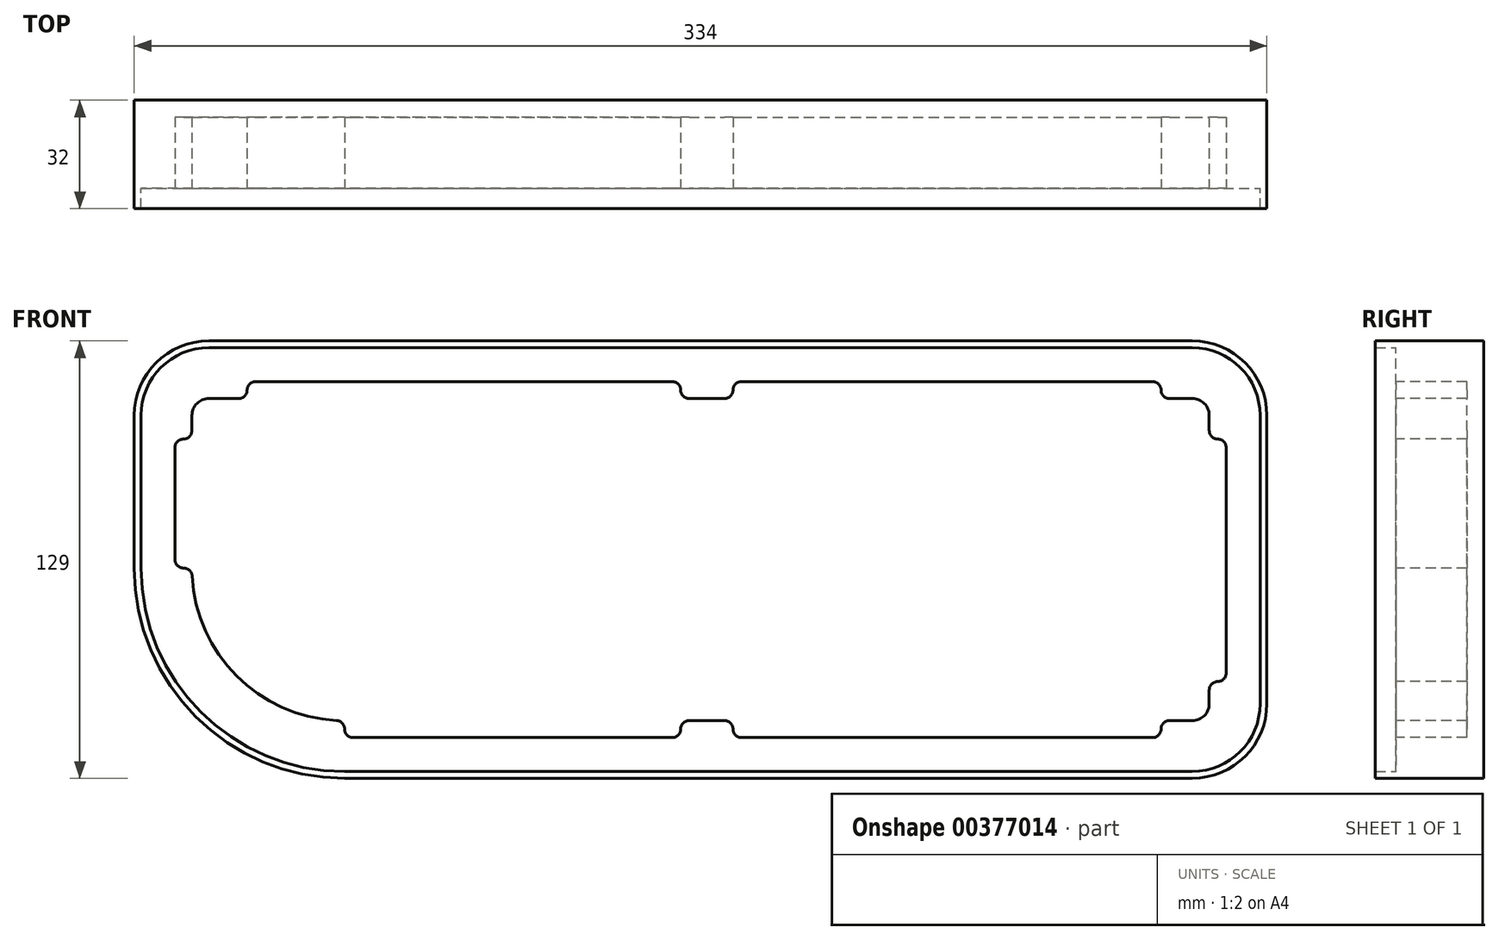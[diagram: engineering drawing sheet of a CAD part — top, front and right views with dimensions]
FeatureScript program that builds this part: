
annotation { "Feature Type Name" : "Feature", "Feature Type Description" : "" }
export const myFeature = defineFeature(function(context is Context, id is Id, definition is map)
    precondition{}
    {
        {
            var Q0;
            Q0=qCreatedBy(makeId("Front.planeOp"),FACE);
            var sketch = newSketch(context, id + "F0", { "sketchPlane" : qUnion([Q0])});
            skLineSegment(sketch, "E0.bottom", {"start": v(55, 0) * mm, "end": v(305, 0) * mm});
            skLineSegment(sketch, "E0.top", {"start": v(15, 115) * mm, "end": v(305, 115) * mm});
            skLineSegment(sketch, "E0.left", {"start": v(0, 55) * mm, "end": v(0, 100) * mm});
            skLineSegment(sketch, "E0.right", {"start": v(320, 15) * mm, "end": v(320, 100) * mm});
            skPoint(sketch, "E1.visualSharp", {"position": v(0, 115) * mm});
            skArc(sketch, "E1.filletArc", {"start": v(15, 115) * mm, "mid": v(4.4, 110.6) * mm, "end": v(0, 100) * mm});
            skPoint(sketch, "E2.visualSharp", {"position": v(320, 115) * mm});
            skArc(sketch, "E2.filletArc", {"start": v(320, 100) * mm, "mid": v(315.6, 110.6) * mm, "end": v(305, 115) * mm});
            skPoint(sketch, "E3.visualSharp", {"position": v(320, 0) * mm});
            skArc(sketch, "E3.filletArc", {"start": v(305, 0) * mm, "mid": v(315.6, 4.4) * mm, "end": v(320, 15) * mm});
            skPoint(sketch, "E4.visualSharp", {"position": v(0, 0) * mm});
            skArc(sketch, "E4.filletArc", {"start": v(0, 55) * mm, "mid": v(16.1, 16.1) * mm, "end": v(55, 0) * mm});
            skArc(sketch, "E5.0", {"start": v(15, 120) * mm, "mid": v(0.86, 114.14) * mm, "end": v(-5, 100) * mm});
            skLineSegment(sketch, "E5.1", {"start": v(-5, 55) * mm, "end": v(-5, 100) * mm});
            skLineSegment(sketch, "E5.2", {"start": v(15, 120) * mm, "end": v(305, 120) * mm});
            skArc(sketch, "E5.3", {"start": v(-5, 55) * mm, "mid": v(12.57, 12.57) * mm, "end": v(55, -5) * mm});
            skArc(sketch, "E5.4", {"start": v(325, 100) * mm, "mid": v(319.14, 114.14) * mm, "end": v(305, 120) * mm});
            skLineSegment(sketch, "E5.5", {"start": v(325, 15) * mm, "end": v(325, 100) * mm});
            skArc(sketch, "E5.6", {"start": v(305, -5) * mm, "mid": v(319.14, 0.86) * mm, "end": v(325, 15) * mm});
            skLineSegment(sketch, "E5.7", {"start": v(55, -5) * mm, "end": v(305, -5) * mm});
            skLineSegment(sketch, "E6", {"start": v(160, 115) * mm, "end": v(164.05, 0) * mm});
            skLineSegment(sketch, "E7", {"start": v(189.87, 0) * mm, "end": v(186.97, 115) * mm});
            skPoint(sketch, "E8.direction1.start.orphan", {"position": v(300, 20) * mm});
            skSolve(sketch);
        }
        {
            var Q0;
            Q0=qCreatedBy(makeId("Front.planeOp"),FACE);
            var sketch = newSketch(context, id + "F1", { "sketchPlane" : qUnion([Q0])});
            skLineSegment(sketch, "E9.0", {"start": v(-5, 55) * mm, "end": v(-5, 100) * mm});
            skArc(sketch, "E10.0", {"start": v(15, 120) * mm, "mid": v(0.86, 114.14) * mm, "end": v(-5, 100) * mm});
            skArc(sketch, "E11.0", {"start": v(-5, 55) * mm, "mid": v(12.57, 12.57) * mm, "end": v(55, -5) * mm});
            skLineSegment(sketch, "E12.0", {"start": v(55, -5) * mm, "end": v(305, -5) * mm});
            skLineSegment(sketch, "E13.0", {"start": v(15, 120) * mm, "end": v(305, 120) * mm});
            skPoint(sketch, "E14.0", {"position": v(320, 115) * mm});
            skPoint(sketch, "E15.0", {"position": v(319.14, 114.14) * mm});
            skArc(sketch, "E16.0", {"start": v(325, 100) * mm, "mid": v(319.14, 114.14) * mm, "end": v(305, 120) * mm});
            skLineSegment(sketch, "E17.0", {"start": v(325, 15) * mm, "end": v(325, 100) * mm});
            skArc(sketch, "E18.0", {"start": v(305, -5) * mm, "mid": v(319.14, 0.86) * mm, "end": v(325, 15) * mm});
            skLineSegment(sketch, "E19.0.5", {"start": v(305, 120) * mm, "end": v(15, 120) * mm});
            skLineSegment(sketch, "E19.0.7", {"start": v(-5, 100) * mm, "end": v(-5, 55) * mm});
            skSolve(sketch);
        }
        {
            var Q0;
            Q0=makeQuery(id+"F1.imprint","IMPRINT",FACE,{"disambiguationData":[TD([[makeQuery(id+"F1.imprint","IMPRINT",EDGE,{"derivedFrom":sQuery(id+"F1.wireOp",EDGE,"E11.0")}),1.0]])]});
            extrude(context, id + "F2", {"entities" : qUnion([Q0]), "depth" : 25 * mm});
        }
        {
            var Q0;
            Q0=makeQuery(id+"F2.opExtrude","CAP_FACE",FACE,{"disambiguationData":[OSD([sQuery(id+"F1.wireOp",EDGE,"E11.0"),sQuery(id+"F1.wireOp",EDGE,"E12.0"),sQuery(id+"F1.wireOp",EDGE,"E18.0"),sQuery(id+"F1.wireOp",EDGE,"E17.0"),sQuery(id+"F1.wireOp",EDGE,"E16.0"),sQuery(id+"F1.wireOp",EDGE,"E19.0.5"),sQuery(id+"F1.wireOp",EDGE,"E10.0"),sQuery(id+"F1.wireOp",EDGE,"E19.0.7")])],"isStart":false});
            var Q1;
            Q1=makeQuery(id+"F0.imprint","IMPRINT",FACE,{"disambiguationData":[TD([[makeQuery(id+"F0.imprint","IMPRINT",EDGE,{"derivedFrom":sQuery(id+"F0.wireOp",EDGE,"E0.right")}),1.0]])]});
            var Q2;
            Q2=makeQuery(id+"F2.opExtrude","CAP_FACE",FACE,{"disambiguationData":[OSD([sQuery(id+"F1.wireOp",EDGE,"E11.0"),sQuery(id+"F1.wireOp",EDGE,"E12.0"),sQuery(id+"F1.wireOp",EDGE,"E18.0"),sQuery(id+"F1.wireOp",EDGE,"E17.0"),sQuery(id+"F1.wireOp",EDGE,"E16.0"),sQuery(id+"F1.wireOp",EDGE,"E19.0.5"),sQuery(id+"F1.wireOp",EDGE,"E10.0"),sQuery(id+"F1.wireOp",EDGE,"E19.0.7")])],"isStart":true});
            extrude(context, id + "F3", {"entities" : qUnion([Q0, Q1, Q2]), "operationType" : NewBodyOperationType.REMOVE, "oppositeDirection" : true, "depth" : 4 * mm});
        }
        {
            var Q0;
            {var subQ0=sQuery(id+"F1.wireOp",EDGE,"E19.0.7");var subQ1=sQuery(id+"F1.wireOp",EDGE,"E10.0");var subQ2=sQuery(id+"F1.wireOp",EDGE,"E19.0.5");var subQ3=sQuery(id+"F1.wireOp",EDGE,"E16.0");var subQ4=sQuery(id+"F1.wireOp",EDGE,"E17.0");var subQ5=sQuery(id+"F1.wireOp",EDGE,"E18.0");var subQ6=sQuery(id+"F1.wireOp",EDGE,"E12.0");var subQ7=sQuery(id+"F1.wireOp",EDGE,"E11.0");Q0=makeQuery(id+"F3.boolean.opBoolean","COPY",FACE,{"derivedFrom":makeQuery(id+"F3.opExtrude","CAP_FACE",FACE,{"disambiguationData":[OSD([subQ7,subQ6,subQ5,subQ4,subQ3,subQ2,subQ1,subQ0]),TDD([makeQuery(id+"F2.opExtrude","CAP_FACE",FACE,{"disambiguationData":[OSD([subQ7,subQ6,subQ5,subQ4,subQ3,subQ2,subQ1,subQ0])],"isStart":false})])],"isStart":false})});}
            var sketch = newSketch(context, id + "F4", { "sketchPlane" : qUnion([Q0])});
            skArc(sketch, "E20.0.5", {"start": v(0, 55) * mm, "mid": v(16.1, 16.1) * mm, "end": v(55, 0) * mm});
            skArc(sketch, "E21.0", {"start": v(305, 10) * mm, "mid": v(308.54, 11.46) * mm, "end": v(310, 15) * mm});
            skLineSegment(sketch, "E21.1", {"start": v(156.6, 10) * mm, "end": v(167.06, 10) * mm});
            skLineSegment(sketch, "E21.2", {"start": v(310, 15) * mm, "end": v(310, 19.03) * mm});
            skArc(sketch, "E21.3", {"start": v(10.06, 52.63) * mm, "mid": v(23.18, 23.18) * mm, "end": v(52.63, 10.06) * mm});
            skArc(sketch, "E21.4", {"start": v(310, 100) * mm, "mid": v(308.54, 103.54) * mm, "end": v(305, 105) * mm});
            skLineSegment(sketch, "E21.5", {"start": v(305, 105) * mm, "end": v(298.29, 105) * mm});
            skArc(sketch, "E21.6", {"start": v(15, 105) * mm, "mid": v(11.46, 103.54) * mm, "end": v(10, 100) * mm});
            skLineSegment(sketch, "E21.7", {"start": v(10, 100) * mm, "end": v(10, 95.55) * mm});
            skPoint(sketch, "E20.0.3.start.orphan", {"position": v(15, 115) * mm});
            skPoint(sketch, "E20.0.4.start.orphan", {"position": v(0, 100) * mm});
            skPoint(sketch, "E20.0.1.end.orphan", {"position": v(305, 115) * mm});
            skPoint(sketch, "E20.0.0.end.orphan", {"position": v(320, 100) * mm});
            skPoint(sketch, "E20.0.7.end.orphan", {"position": v(320, 15) * mm});
            skPoint(sketch, "E20.0.6.end.orphan", {"position": v(305, 0) * mm});
            skLineSegment(sketch, "E22.1", {"start": v(315, 24.03) * mm, "end": v(315, 90.55) * mm});
            skLineSegment(sketch, "E22.2", {"start": v(293.29, 110) * mm, "end": v(172.06, 110) * mm});
            skLineSegment(sketch, "E22.5", {"start": v(5, 90.55) * mm, "end": v(5, 57.5) * mm});
            skLineSegment(sketch, "E22.7", {"start": v(57.5, 5) * mm, "end": v(151.6, 5) * mm});
            skLineSegment(sketch, "E23", {"start": v(295.79, 107.5) * mm, "end": v(295.79, 107.5) * mm});
            skLineSegment(sketch, "E24", {"start": v(169.56, 107.5) * mm, "end": v(169.56, 107.5) * mm});
            skLineSegment(sketch, "E25", {"start": v(154.1, 107.5) * mm, "end": v(154.1, 107.5) * mm});
            skLineSegment(sketch, "E26", {"start": v(26.27, 107.5) * mm, "end": v(26.27, 107.5) * mm});
            skLineSegment(sketch, "E27", {"start": v(7.5, 93.05) * mm, "end": v(7.5, 93.05) * mm});
            skLineSegment(sketch, "E28", {"start": v(7.57, 55) * mm, "end": v(7.5, 55) * mm});
            skLineSegment(sketch, "E29", {"start": v(55, 7.57) * mm, "end": v(55, 7.5) * mm});
            skLineSegment(sketch, "E30", {"start": v(154.1, 7.5) * mm, "end": v(154.1, 7.5) * mm});
            skLineSegment(sketch, "E31", {"start": v(169.56, 7.5) * mm, "end": v(169.56, 7.5) * mm});
            skLineSegment(sketch, "E32", {"start": v(295.79, 7.5) * mm, "end": v(295.79, 7.5) * mm});
            skLineSegment(sketch, "E33", {"start": v(312.5, 93.05) * mm, "end": v(312.5, 93.05) * mm});
            skLineSegment(sketch, "E34", {"start": v(312.5, 21.53) * mm, "end": v(312.5, 21.53) * mm});
            skLineSegment(sketch, "E35.trimOffspring", {"start": v(23.77, 105) * mm, "end": v(15, 105) * mm});
            skLineSegment(sketch, "E36.trimOffspring", {"start": v(151.6, 110) * mm, "end": v(28.77, 110) * mm});
            skLineSegment(sketch, "E37.trimOffspring", {"start": v(167.06, 105) * mm, "end": v(156.6, 105) * mm});
            skLineSegment(sketch, "E38.trimOffspring", {"start": v(310, 95.55) * mm, "end": v(310, 100) * mm});
            skLineSegment(sketch, "E39.trimOffspring", {"start": v(298.29, 10) * mm, "end": v(305, 10) * mm});
            skLineSegment(sketch, "E40.trimOffspring", {"start": v(172.06, 5) * mm, "end": v(293.29, 5) * mm});
            skPoint(sketch, "E41.visualSharp", {"position": v(10, 93.05) * mm});
            skArc(sketch, "E41.filletArc", {"start": v(7.5, 93.05) * mm, "mid": v(9.27, 93.78) * mm, "end": v(10, 95.55) * mm});
            skPoint(sketch, "E42.visualSharp", {"position": v(5, 93.05) * mm});
            skArc(sketch, "E42.filletArc", {"start": v(7.5, 93.05) * mm, "mid": v(5.73, 92.32) * mm, "end": v(5, 90.55) * mm});
            skPoint(sketch, "E43.visualSharp", {"position": v(26.27, 105) * mm});
            skArc(sketch, "E43.filletArc", {"start": v(23.77, 105) * mm, "mid": v(25.54, 105.73) * mm, "end": v(26.27, 107.5) * mm});
            skPoint(sketch, "E44.visualSharp", {"position": v(26.27, 110) * mm});
            skArc(sketch, "E44.filletArc", {"start": v(28.77, 110) * mm, "mid": v(27, 109.27) * mm, "end": v(26.27, 107.5) * mm});
            skPoint(sketch, "E45.visualSharp", {"position": v(5, 55) * mm});
            skArc(sketch, "E45.filletArc", {"start": v(5, 57.5) * mm, "mid": v(5.73, 55.73) * mm, "end": v(7.5, 55) * mm});
            skPoint(sketch, "E46.visualSharp", {"position": v(10, 55) * mm});
            skArc(sketch, "E46.filletArc", {"start": v(10.06, 52.63) * mm, "mid": v(9.29, 54.31) * mm, "end": v(7.57, 55) * mm});
            skPoint(sketch, "E47.visualSharp", {"position": v(55, 10) * mm});
            skArc(sketch, "E47.filletArc", {"start": v(55, 7.57) * mm, "mid": v(54.31, 9.29) * mm, "end": v(52.63, 10.06) * mm});
            skPoint(sketch, "E48.visualSharp", {"position": v(55, 5) * mm});
            skArc(sketch, "E48.filletArc", {"start": v(55, 7.5) * mm, "mid": v(55.73, 5.73) * mm, "end": v(57.5, 5) * mm});
            skPoint(sketch, "E49.visualSharp", {"position": v(154.1, 5) * mm});
            skArc(sketch, "E49.filletArc", {"start": v(151.6, 5) * mm, "mid": v(153.38, 5.73) * mm, "end": v(154.1, 7.5) * mm});
            skPoint(sketch, "E50.visualSharp", {"position": v(154.1, 10) * mm});
            skArc(sketch, "E50.filletArc", {"start": v(156.6, 10) * mm, "mid": v(154.84, 9.27) * mm, "end": v(154.1, 7.5) * mm});
            skPoint(sketch, "E51.visualSharp", {"position": v(169.56, 10) * mm});
            skArc(sketch, "E51.filletArc", {"start": v(169.56, 7.5) * mm, "mid": v(168.83, 9.27) * mm, "end": v(167.06, 10) * mm});
            skPoint(sketch, "E52.visualSharp", {"position": v(169.56, 5) * mm});
            skArc(sketch, "E52.filletArc", {"start": v(169.56, 7.5) * mm, "mid": v(170.3, 5.73) * mm, "end": v(172.06, 5) * mm});
            skPoint(sketch, "E53.visualSharp", {"position": v(295.79, 5) * mm});
            skArc(sketch, "E53.filletArc", {"start": v(293.29, 5) * mm, "mid": v(295.05, 5.73) * mm, "end": v(295.79, 7.5) * mm});
            skPoint(sketch, "E54.visualSharp", {"position": v(295.79, 10) * mm});
            skArc(sketch, "E54.filletArc", {"start": v(298.29, 10) * mm, "mid": v(296.52, 9.27) * mm, "end": v(295.79, 7.5) * mm});
            skPoint(sketch, "E55.visualSharp", {"position": v(310, 21.53) * mm});
            skArc(sketch, "E55.filletArc", {"start": v(312.5, 21.53) * mm, "mid": v(310.73, 20.8) * mm, "end": v(310, 19.03) * mm});
            skPoint(sketch, "E56.visualSharp", {"position": v(315, 21.53) * mm});
            skArc(sketch, "E56.filletArc", {"start": v(312.5, 21.53) * mm, "mid": v(314.27, 22.26) * mm, "end": v(315, 24.03) * mm});
            skPoint(sketch, "E57.visualSharp", {"position": v(315, 93.05) * mm});
            skArc(sketch, "E57.filletArc", {"start": v(315, 90.55) * mm, "mid": v(314.27, 92.32) * mm, "end": v(312.5, 93.05) * mm});
            skPoint(sketch, "E58.visualSharp", {"position": v(310, 93.05) * mm});
            skArc(sketch, "E58.filletArc", {"start": v(310, 95.55) * mm, "mid": v(310.73, 93.78) * mm, "end": v(312.5, 93.05) * mm});
            skPoint(sketch, "E59.visualSharp", {"position": v(295.79, 105) * mm});
            skArc(sketch, "E59.filletArc", {"start": v(295.79, 107.5) * mm, "mid": v(296.52, 105.73) * mm, "end": v(298.29, 105) * mm});
            skPoint(sketch, "E60.visualSharp", {"position": v(295.79, 110) * mm});
            skArc(sketch, "E60.filletArc", {"start": v(295.79, 107.5) * mm, "mid": v(295.05, 109.27) * mm, "end": v(293.29, 110) * mm});
            skPoint(sketch, "E61.visualSharp", {"position": v(169.56, 110) * mm});
            skArc(sketch, "E61.filletArc", {"start": v(172.06, 110) * mm, "mid": v(170.3, 109.27) * mm, "end": v(169.56, 107.5) * mm});
            skPoint(sketch, "E62.visualSharp", {"position": v(169.56, 105) * mm});
            skArc(sketch, "E62.filletArc", {"start": v(167.06, 105) * mm, "mid": v(168.83, 105.73) * mm, "end": v(169.56, 107.5) * mm});
            skPoint(sketch, "E63.visualSharp", {"position": v(154.1, 105) * mm});
            skArc(sketch, "E63.filletArc", {"start": v(154.1, 107.5) * mm, "mid": v(154.84, 105.73) * mm, "end": v(156.6, 105) * mm});
            skPoint(sketch, "E64.visualSharp", {"position": v(154.1, 110) * mm});
            skArc(sketch, "E64.filletArc", {"start": v(154.1, 107.5) * mm, "mid": v(153.38, 109.27) * mm, "end": v(151.6, 110) * mm});
            skSolve(sketch);
        }
        {
            var Q0;
            Q0=makeQuery(id+"F4.imprint","IMPRINT",FACE,{"disambiguationData":[TD([[makeQuery(id+"F4.imprint","IMPRINT",EDGE,{"derivedFrom":sQuery(id+"F4.wireOp",EDGE,"E21.0")}),1.0]])]});
            extrude(context, id + "F5", {"entities" : qUnion([Q0]), "operationType" : NewBodyOperationType.REMOVE, "oppositeDirection" : true, "depth" : 25 * mm});
        }
        {
            var Q0;
            Q0=makeQuery(id+"F2.opExtrude","CAP_FACE",FACE,{"disambiguationData":[OSD([sQuery(id+"F1.wireOp",EDGE,"E11.0"),sQuery(id+"F1.wireOp",EDGE,"E12.0"),sQuery(id+"F1.wireOp",EDGE,"E18.0"),sQuery(id+"F1.wireOp",EDGE,"E17.0"),sQuery(id+"F1.wireOp",EDGE,"E16.0"),sQuery(id+"F1.wireOp",EDGE,"E19.0.5"),sQuery(id+"F1.wireOp",EDGE,"E10.0"),sQuery(id+"F1.wireOp",EDGE,"E19.0.7")])],"isStart":true});
            var sketch = newSketch(context, id + "F6", { "sketchPlane" : qUnion([Q0])});
            skPoint(sketch, "E65.0", {"position": v(-319.14, 114.14) * mm});
            skPoint(sketch, "E66.0", {"position": v(-0.86, 114.14) * mm});
            skLineSegment(sketch, "E67.0", {"start": v(7, 100) * mm, "end": v(7, 55) * mm});
            skArc(sketch, "E67.1", {"start": v(-15, 122) * mm, "mid": v(0.56, 115.56) * mm, "end": v(7, 100) * mm});
            skArc(sketch, "E67.2", {"start": v(7, 55) * mm, "mid": v(-11.16, 11.16) * mm, "end": v(-55, -7) * mm});
            skLineSegment(sketch, "E67.3", {"start": v(-305, 122) * mm, "end": v(-15, 122) * mm});
            skLineSegment(sketch, "E67.4", {"start": v(-55, -7) * mm, "end": v(-305, -7) * mm});
            skArc(sketch, "E67.5", {"start": v(-305, -7) * mm, "mid": v(-320.56, -0.56) * mm, "end": v(-327, 15) * mm});
            skLineSegment(sketch, "E67.6", {"start": v(-327, 15) * mm, "end": v(-327, 100) * mm});
            skArc(sketch, "E67.7", {"start": v(-327, 100) * mm, "mid": v(-320.56, 115.56) * mm, "end": v(-305, 122) * mm});
            skPoint(sketch, "E68.orphan", {"position": v(-305, 120) * mm});
            skPoint(sketch, "E69.0.end.orphan", {"position": v(-325, 100) * mm});
            skPoint(sketch, "E70.0.end.orphan", {"position": v(-325, 15) * mm});
            skPoint(sketch, "E71.0.end.orphan", {"position": v(-305, -5) * mm});
            skPoint(sketch, "E72.0.end.orphan", {"position": v(-55, -5) * mm});
            skPoint(sketch, "E73.0.end.orphan", {"position": v(5, 55) * mm});
            skPoint(sketch, "E74.orphan", {"position": v(5, 100) * mm});
            skPoint(sketch, "E75.0.start.orphan", {"position": v(-15, 120) * mm});
            skSolve(sketch);
        }
        {
            var Q0;
            Q0 = qSketchRegion(id + "F6", true);
            extrude(context, id + "F7", {"entities" : qUnion([Q0]), "operationType" : NewBodyOperationType.ADD, "depth" : 5 * mm});
        }
        {
            var Q0;
            Q0=makeQuery(id+"F7.boolean.opBoolean","SPLIT",FACE,{"disambiguationData":[TD([makeQuery(id+"F5.boolean.opBoolean","COPY",FACE,{"derivedFrom":makeQuery(id+"F5.opExtrude","SWEPT_FACE",FACE,{"disambiguationData":[OSD([sQuery(id+"F4.wireOp",EDGE,"E21.0")])]})})])],"derivedFrom":makeQuery(id+"F7.opExtrude","CAP_FACE",FACE,{"disambiguationData":[OSD([sQuery(id+"F6.wireOp",EDGE,"E67.0"),sQuery(id+"F6.wireOp",EDGE,"E67.1"),sQuery(id+"F6.wireOp",EDGE,"E67.2"),sQuery(id+"F6.wireOp",EDGE,"E67.3"),sQuery(id+"F6.wireOp",EDGE,"E67.4"),sQuery(id+"F6.wireOp",EDGE,"E67.5"),sQuery(id+"F6.wireOp",EDGE,"E67.6"),sQuery(id+"F6.wireOp",EDGE,"E67.7")])],"isStart":true})});
            var sketch = newSketch(context, id + "F8", { "sketchPlane" : qUnion([Q0])});
            skArc(sketch, "E76.0.0", {"start": v(327, 100) * mm, "mid": v(320.56, 115.56) * mm, "end": v(305, 122) * mm});
            skLineSegment(sketch, "E76.0.1", {"start": v(305, 122) * mm, "end": v(15, 122) * mm});
            skArc(sketch, "E76.0.2", {"start": v(15, 122) * mm, "mid": v(-0.56, 115.56) * mm, "end": v(-7, 100) * mm});
            skLineSegment(sketch, "E76.0.3", {"start": v(-7, 100) * mm, "end": v(-7, 55) * mm});
            skArc(sketch, "E76.0.4", {"start": v(-7, 55) * mm, "mid": v(11.16, 11.16) * mm, "end": v(55, -7) * mm});
            skLineSegment(sketch, "E76.0.5", {"start": v(55, -7) * mm, "end": v(305, -7) * mm});
            skArc(sketch, "E76.0.6", {"start": v(305, -7) * mm, "mid": v(320.56, -0.56) * mm, "end": v(327, 15) * mm});
            skLineSegment(sketch, "E76.0.7", {"start": v(327, 15) * mm, "end": v(327, 100) * mm});
            skArc(sketch, "E77.0", {"start": v(15, 120) * mm, "mid": v(0.86, 114.14) * mm, "end": v(-5, 100) * mm});
            skLineSegment(sketch, "E78.0", {"start": v(-5, 100) * mm, "end": v(-5, 55) * mm});
            skArc(sketch, "E79.0", {"start": v(-5, 55) * mm, "mid": v(12.57, 12.57) * mm, "end": v(55, -5) * mm});
            skLineSegment(sketch, "E80.0", {"start": v(55, -5) * mm, "end": v(305, -5) * mm});
            skLineSegment(sketch, "E81.0", {"start": v(305, 120) * mm, "end": v(15, 120) * mm});
            skArc(sketch, "E82.0", {"start": v(325, 100) * mm, "mid": v(319.14, 114.14) * mm, "end": v(305, 120) * mm});
            skLineSegment(sketch, "E83.0", {"start": v(325, 15) * mm, "end": v(325, 100) * mm});
            skArc(sketch, "E84.0", {"start": v(305, -5) * mm, "mid": v(319.14, 0.86) * mm, "end": v(325, 15) * mm});
            skSolve(sketch);
        }
        {
            var Q0;
            Q0 = qSketchRegion(id + "F8", true);
            extrude(context, id + "F9", {"entities" : qUnion([Q0]), "operationType" : NewBodyOperationType.ADD, "depth" : 27 * mm});
        }
    });
